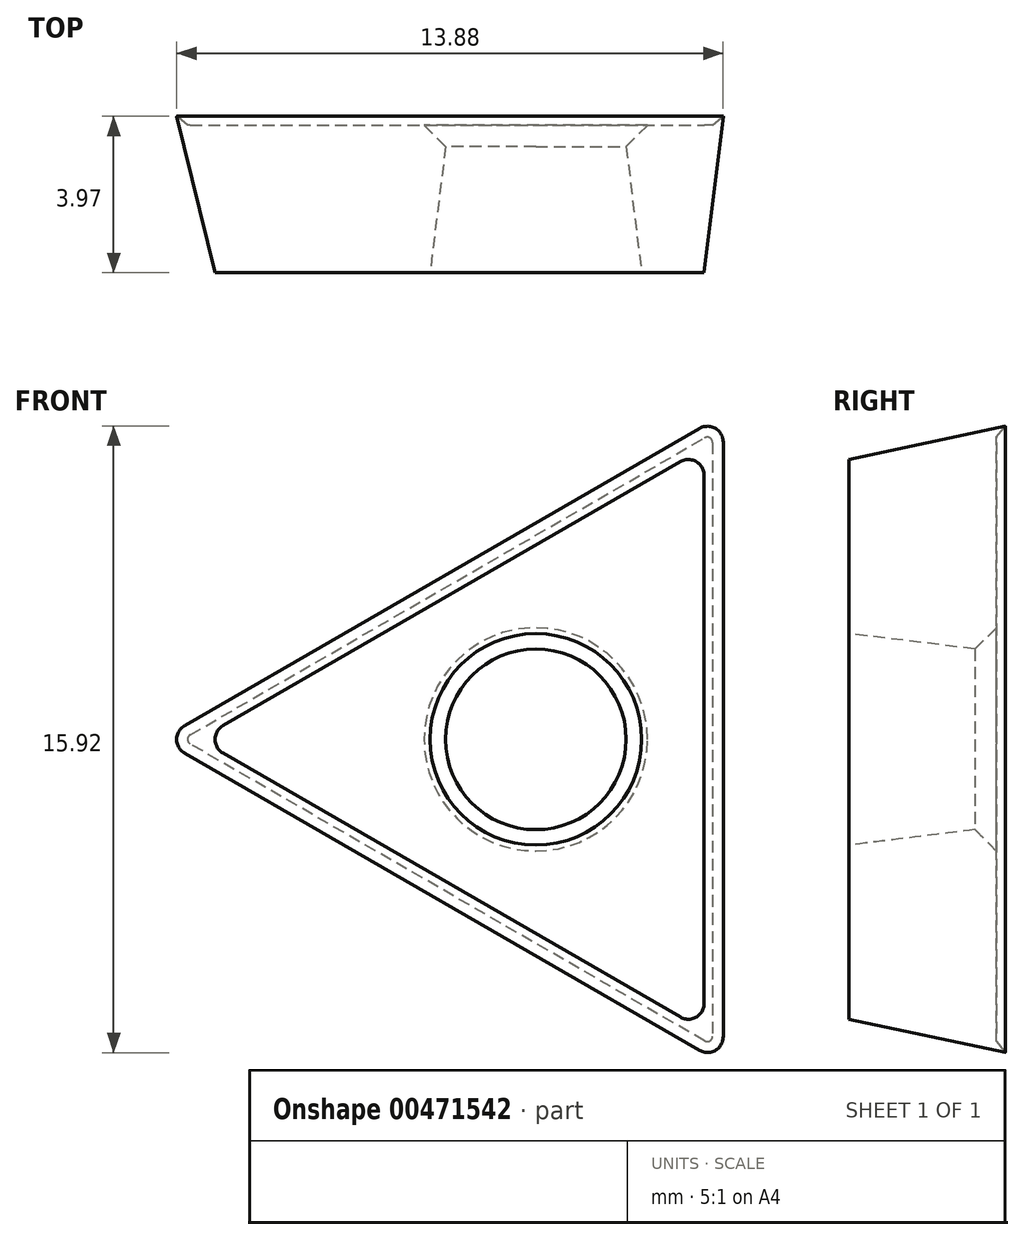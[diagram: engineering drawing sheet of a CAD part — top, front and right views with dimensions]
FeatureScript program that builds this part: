
annotation { "Feature Type Name" : "Feature", "Feature Type Description" : "" }
export const myFeature = defineFeature(function(context is Context, id is Id, definition is map)
    precondition{}
    {
        {
            var Q0;
            Q0=qCreatedBy(makeId("Front.planeOp"),FACE);
            var sketch = newSketch(context, id + "F0", { "sketchPlane" : qUnion([Q0])});
            skCircle(sketch, "E0.cCircle", {"center": v(0, 0) * mm, "radius": 4.76 * mm, "construction": true});
            skPoint(sketch, "E0.0.midPoint", {"position": v(4.76, 0) * mm});
            skPoint(sketch, "E1.visualSharp", {"position": v(-9.52, 0) * mm});
            skPoint(sketch, "E2.visualSharp", {"position": v(4.76, 8.25) * mm});
            skPoint(sketch, "E3.visualSharp", {"position": v(4.76, -8.25) * mm});
            skCircle(sketch, "E4", {"center": v(0, 0) * mm, "radius": 2.2 * mm});
            skLineSegment(sketch, "E5", {"start": v(-9.52, 0) * mm, "end": v(4.76, 8.25) * mm});
            skLineSegment(sketch, "E6", {"start": v(4.76, 8.25) * mm, "end": v(4.76, -8.25) * mm});
            skLineSegment(sketch, "E7", {"start": v(4.76, -8.25) * mm, "end": v(-9.52, 0) * mm});
            skSolve(sketch);
        }
        {
            var Q0;
            Q0=makeQuery(id+"F0.imprint","IMPRINT",FACE,{"disambiguationData":[TD([[makeQuery(id+"F0.imprint","IMPRINT",EDGE,{"derivedFrom":sQuery(id+"F0.wireOp",EDGE,"E0.0")}),-1.0]])]});
            var Q1;
            Q1=makeQuery(id+"F0.imprint","IMPRINT",FACE,{"disambiguationData":[TD([[makeQuery(id+"F0.imprint","IMPRINT",EDGE,{"derivedFrom":sQuery(id+"F0.wireOp",EDGE,"E4")}),-1.0]])]});
            extrude(context, id + "F1", {"entities" : qUnion([Q0, Q1]), "depth" : 3.97 * mm, "hasDraft" : true, "draftAngle" : 7 * degree, "draftPullDirection" : true});
        }
        {
            var Q0;
            Q0=makeQuery(id+"F1.opExtrude","SWEPT_EDGE",EDGE,{"disambiguationData":[OSD([sQuery(id+"F0.wireOp",EDGE,"E5"),sQuery(id+"F0.wireOp",EDGE,"E7")])]});
            var Q1;
            Q1=makeQuery(id+"F1.opExtrude","SWEPT_EDGE",EDGE,{"disambiguationData":[OSD([sQuery(id+"F0.wireOp",EDGE,"E5"),sQuery(id+"F0.wireOp",EDGE,"E6")])]});
            var Q2;
            Q2=makeQuery(id+"F1.opExtrude","SWEPT_EDGE",EDGE,{"disambiguationData":[OSD([sQuery(id+"F0.wireOp",EDGE,"E6"),sQuery(id+"F0.wireOp",EDGE,"E7")])]});
            fillet(context, id + "F2", {"entities" : qUnion([Q0, Q1, Q2]), "radius" : 0.4 * mm, "tangentPropagation" : true, "allowEdgeOverflow" : false});
        }
        {
            var Q0;
            Q0=makeQuery(id+"F0.imprint","IMPRINT",FACE,{"disambiguationData":[TD([[makeQuery(id+"F0.imprint","IMPRINT",EDGE,{"derivedFrom":sQuery(id+"F0.wireOp",EDGE,"E4")}),-1.0]])]});
            var sketch = newSketch(context, id + "F3", { "sketchPlane" : qUnion([Q0])});
            skCircle(sketch, "E8", {"center": v(0, 0) * mm, "radius": 3.07 * mm});
            skSolve(sketch);
        }
        {
            var Q0;
            Q0 = qSketchRegion(id + "F3", true);
            extrude(context, id + "F4", {"entities" : qUnion([Q0]), "operationType" : NewBodyOperationType.REMOVE, "depth" : 1.27 * mm, "hasDraft" : true, "draftAngle" : 45 * degree, "draftPullDirection" : true});
        }
        {
            var Q0;
            Q0=makeQuery(id+"F3.imprint","IMPRINT",FACE,{"disambiguationData":[TD([[makeQuery(id+"F3.imprint","IMPRINT",EDGE,{"derivedFrom":sQuery(id+"F3.wireOp",EDGE,"E8")}),-1.0]])]});
            var sketch = newSketch(context, id + "F5", { "sketchPlane" : qUnion([Q0])});
            skPoint(sketch, "E9.0", {"position": v(4.76, 8.25) * mm});
            skPoint(sketch, "E10.0", {"position": v(4.76, -8.25) * mm});
            skPoint(sketch, "E11.0", {"position": v(-9.52, 0) * mm});
            skLineSegment(sketch, "E12", {"start": v(4.15, 7.9) * mm, "end": v(-8.92, 0.35) * mm});
            skLineSegment(sketch, "E13", {"start": v(4.76, -7.54) * mm, "end": v(4.76, 7.54) * mm});
            skArc(sketch, "E14.filletArc", {"start": v(4.76, 7.54) * mm, "mid": v(4.56, 7.9) * mm, "end": v(4.15, 7.9) * mm});
            skLineSegment(sketch, "E15", {"start": v(-8.92, -0.35) * mm, "end": v(4.15, -7.9) * mm});
            skArc(sketch, "E16.filletArc", {"start": v(-8.92, 0.35) * mm, "mid": v(-9.12, 0) * mm, "end": v(-8.92, -0.35) * mm});
            skArc(sketch, "E17.filletArc", {"start": v(4.15, -7.9) * mm, "mid": v(4.56, -7.9) * mm, "end": v(4.76, -7.54) * mm});
            skSolve(sketch);
        }
        {
            var Q0;
            Q0 = qSketchRegion(id + "F5", true);
            extrude(context, id + "F6", {"entities" : qUnion([Q0]), "operationType" : NewBodyOperationType.REMOVE, "depth" : 0.23 * mm, "hasDraft" : true, "draftAngle" : 50 * degree, "draftPullDirection" : true});
        }
    });
